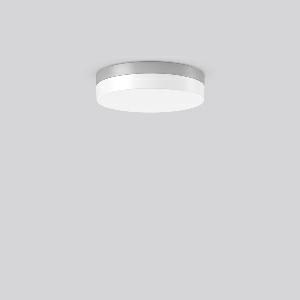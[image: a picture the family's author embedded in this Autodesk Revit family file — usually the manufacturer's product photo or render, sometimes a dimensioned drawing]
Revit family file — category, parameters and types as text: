
# Revit family: flat_slim_round_312674_004_19_8f0a
name_source: partatom
category: Lighting Fixtures
units: mm (PartAtom-declared; Revit-internal decimal feet)

## family parameters
Cut with Voids When Loaded = No
Host = Face
Light Source = No
Part Type = Normal
Room Calculation Point = No
Round Connector Dimension = Use Diameter
Shared = No

## types (1)
- MultiLumen 1 830 (1 x LED Modul 830, 1300 lm, 3000)
    Apparent Load = 11 VA
    CIE Flux Codes = 39 70 89 83 100
    Color Rendering = 80
    Color Temperature = 3000
    Default Elevation = 1800 mm
    Height = 70 mm
    Lamp = 1 x LED Modul 830
    Lamp Light Flux = 1300 lm
    Lamp count = 1
    Length = 300 mm
    Lifetime = 50000 h
    Luminous efficacy = 118 lm/W
    Manufacturer = RZB
    ModVariant = No
    Model = 312674.004.19
    Mounting Place = Ceiling
    Mounting Type = Surface mounted
    Number of Poles = 1
    OnlyDefault = Yes
    Power Factor = 1
    Product Name = FLAT SLIM round
    Product group = Surface mounted ceiling and wall luminaires
    ProductGroupID = 305
    Protection Class = Protection class I
    Protection Degree = Degree of protection
    RLX_Detail_Level = 1
    RLX_Emergency_Light_Flux = 0 lm
    RLX_Emergency_Type = 0
    RLX_Emergency_Type_DB = No
    RlxData = <blob elided: 17297 chars, md5=91423630>
    Socket = socket
    Standby Power = 0 W
    System Light Flux = 1300 lm
    System Power = 11 W
    Type Comments = MultiLumen 1 830
    Type Image = 312629.004.jpg
    URL = http://relux.com
    VarID = multilumen_1_830
    Voltage = 0 V
    Weight = 0.00 kg
    Width = 0 mm  [stored 0 ft]

note: [stored X ft] marks values corroborated as IEEE doubles in the binary element streams (Revit-internal decimal feet)

## geometry (parser evidence)
native form markers: Blend x4, Sweep x13
no freeform markers — native parametric forms only
